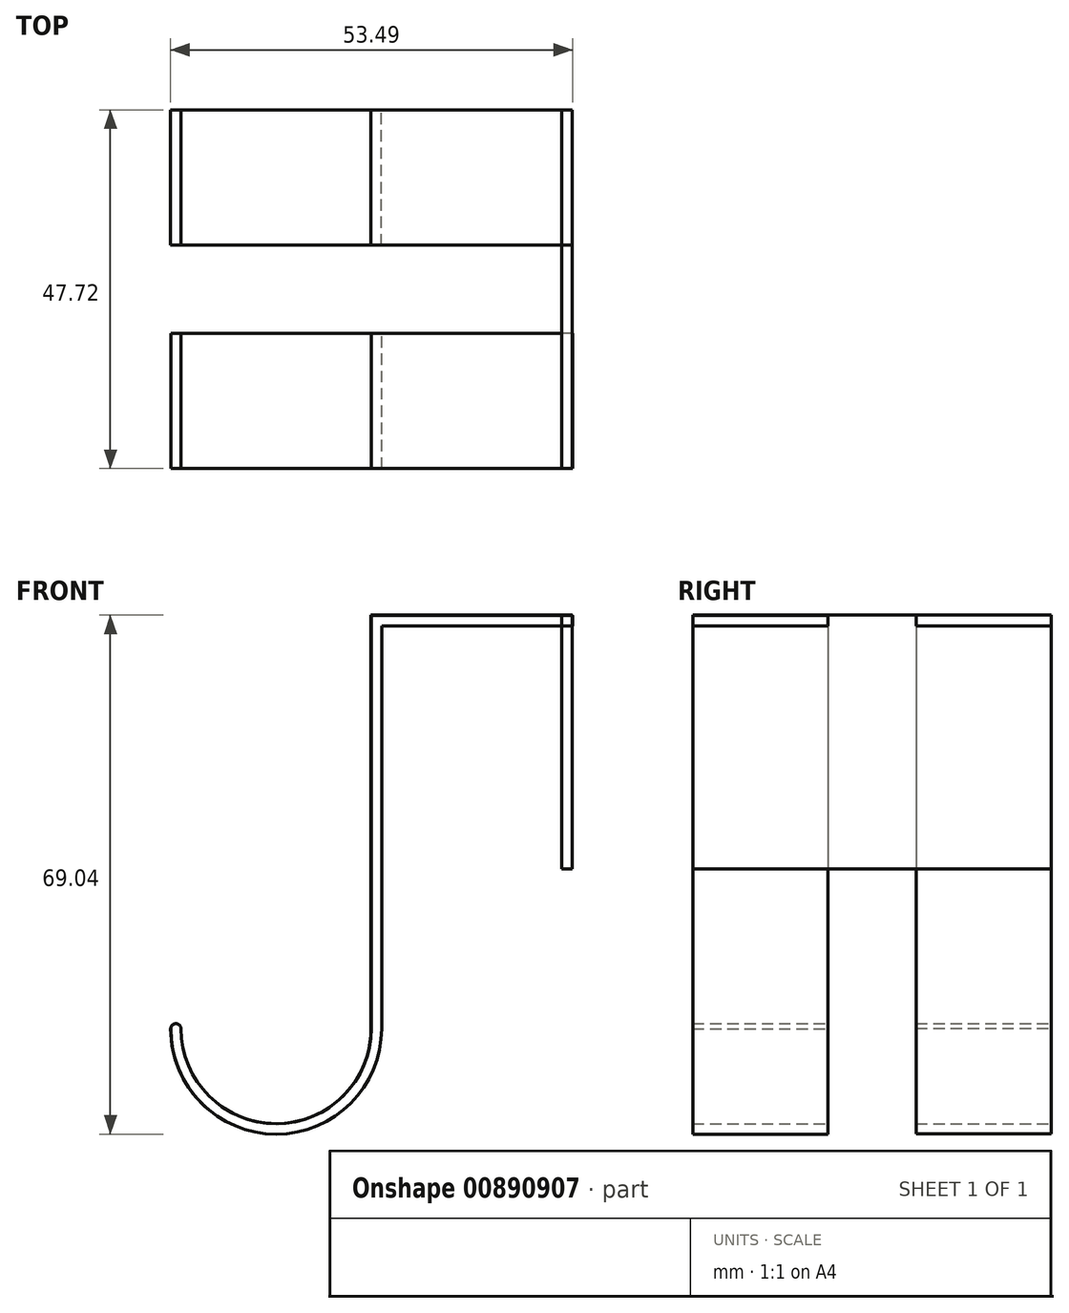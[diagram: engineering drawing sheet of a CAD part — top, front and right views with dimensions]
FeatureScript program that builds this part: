
annotation { "Feature Type Name" : "Feature", "Feature Type Description" : "" }
export const myFeature = defineFeature(function(context is Context, id is Id, definition is map)
    precondition{}
    {
        {
            var Q0;
            Q0=qCreatedBy(makeId("Front.planeOp"),FACE);
            var sketch = newSketch(context, id + "F0", { "sketchPlane" : qUnion([Q0])});
            skLineSegment(sketch, "E0.bottom", {"start": v(-13.36, 58.53) * mm, "end": v(-38.76, 58.53) * mm});
            skLineSegment(sketch, "E0.top", {"start": v(-13.36, 57.1) * mm, "end": v(-38.76, 57.1) * mm});
            skLineSegment(sketch, "E0.right", {"start": v(-38.76, 58.53) * mm, "end": v(-38.76, 57.1) * mm});
            skLineSegment(sketch, "E1.bottom", {"start": v(-38.76, 58.53) * mm, "end": v(-40.15, 58.53) * mm});
            skLineSegment(sketch, "E1.top", {"start": v(-38.76, 3.53) * mm, "end": v(-40.15, 3.53) * mm});
            skLineSegment(sketch, "E1.left", {"start": v(-38.76, 58.53) * mm, "end": v(-38.76, 3.53) * mm});
            skLineSegment(sketch, "E1.right", {"start": v(-40.15, 58.53) * mm, "end": v(-40.15, 3.53) * mm});
            skArc(sketch, "E2", {"start": v(-65.45, 3.53) * mm, "mid": v(-52.8, -9.12) * mm, "end": v(-40.15, 3.53) * mm});
            skArc(sketch, "E3", {"start": v(-66.83, 3.53) * mm, "mid": v(-52.8, -10.5) * mm, "end": v(-38.76, 3.53) * mm});
            skLineSegment(sketch, "E4", {"start": v(-66.83, 3.53) * mm, "end": v(-65.45, 3.53) * mm});
            skArc(sketch, "E5", {"start": v(-65.45, 3.53) * mm, "mid": v(-66.14, 4.18) * mm, "end": v(-66.83, 3.53) * mm});
            skLineSegment(sketch, "E6", {"start": v(-13.36, 58.53) * mm, "end": v(-13.36, 57.1) * mm});
            skSolve(sketch);
        }
        {
            var Q0;
            Q0 = qSketchRegion(id + "F0", true);
            extrude(context, id + "F1", {"entities" : qUnion([Q0]), "depth" : 18 * mm, "offsetDistance" : 25.4 * mm});
        }
        {
            var Q0;
            Q0=qCreatedBy(makeId("Front.planeOp"),FACE);
            cPlane(context, id + "F2", {"entities" : qUnion([Q0]), "cplaneType" : CPlaneType.OFFSET, "offset" : 29.72 * mm, "oppositeDirection" : true, "width" : 152.4 * mm, "height" : 152.4 * mm});
        }
        {
            var Q0;
            Q0=qCreatedBy(id+"F2.planeOp",FACE);
            var sketch = newSketch(context, id + "F3", { "sketchPlane" : qUnion([Q0])});
            skLineSegment(sketch, "E7.bottom", {"start": v(-13.38, 58.54) * mm, "end": v(-38.78, 58.54) * mm});
            skLineSegment(sketch, "E7.top", {"start": v(-13.38, 57.12) * mm, "end": v(-38.78, 57.12) * mm});
            skLineSegment(sketch, "E7.right", {"start": v(-38.78, 58.54) * mm, "end": v(-38.78, 57.12) * mm});
            skLineSegment(sketch, "E8.bottom", {"start": v(-38.78, 58.54) * mm, "end": v(-40.17, 58.54) * mm});
            skLineSegment(sketch, "E8.top", {"start": v(-38.78, 3.54) * mm, "end": v(-40.17, 3.54) * mm});
            skLineSegment(sketch, "E8.left", {"start": v(-38.78, 58.54) * mm, "end": v(-38.78, 3.54) * mm});
            skLineSegment(sketch, "E8.right", {"start": v(-40.17, 58.54) * mm, "end": v(-40.17, 3.54) * mm});
            skArc(sketch, "E9", {"start": v(-65.46, 3.54) * mm, "mid": v(-52.81, -9.1) * mm, "end": v(-40.17, 3.54) * mm});
            skArc(sketch, "E10", {"start": v(-66.85, 3.54) * mm, "mid": v(-52.81, -10.5) * mm, "end": v(-38.78, 3.54) * mm});
            skLineSegment(sketch, "E11", {"start": v(-66.85, 3.54) * mm, "end": v(-65.46, 3.54) * mm});
            skArc(sketch, "E12", {"start": v(-65.46, 3.54) * mm, "mid": v(-66.15, 4.2) * mm, "end": v(-66.85, 3.54) * mm});
            skLineSegment(sketch, "E13", {"start": v(-13.38, 58.54) * mm, "end": v(-13.38, 57.12) * mm});
            skSolve(sketch);
        }
        {
            var Q0;
            Q0 = qSketchRegion(id + "F3", true);
            extrude(context, id + "F4", {"entities" : qUnion([Q0]), "depth" : 18 * mm, "offsetDistance" : 25.4 * mm});
        }
        {
            var Q0;
            Q0=makeQuery(id+"F4.opExtrude","SWEPT_FACE",FACE,{"disambiguationData":[OSD([sQuery(id+"F3.wireOp",EDGE,"E13")])]});
            var sketch = newSketch(context, id + "F5", { "sketchPlane" : qUnion([Q0])});
            skLineSegment(sketch, "E14.bottom", {"start": v(-18, 58.54) * mm, "end": v(29.72, 58.54) * mm});
            skLineSegment(sketch, "E14.top", {"start": v(-18, 24.8) * mm, "end": v(29.72, 24.8) * mm});
            skLineSegment(sketch, "E14.left", {"start": v(-18, 58.54) * mm, "end": v(-18, 24.8) * mm});
            skLineSegment(sketch, "E14.right", {"start": v(29.72, 58.54) * mm, "end": v(29.72, 24.8) * mm});
            skSolve(sketch);
        }
        {
            var Q0;
            Q0 = qSketchRegion(id + "F5", true);
            extrude(context, id + "F6", {"entities" : qUnion([Q0]), "oppositeDirection" : true, "depth" : 1.43 * mm, "offsetDistance" : 25.4 * mm});
        }
    });
